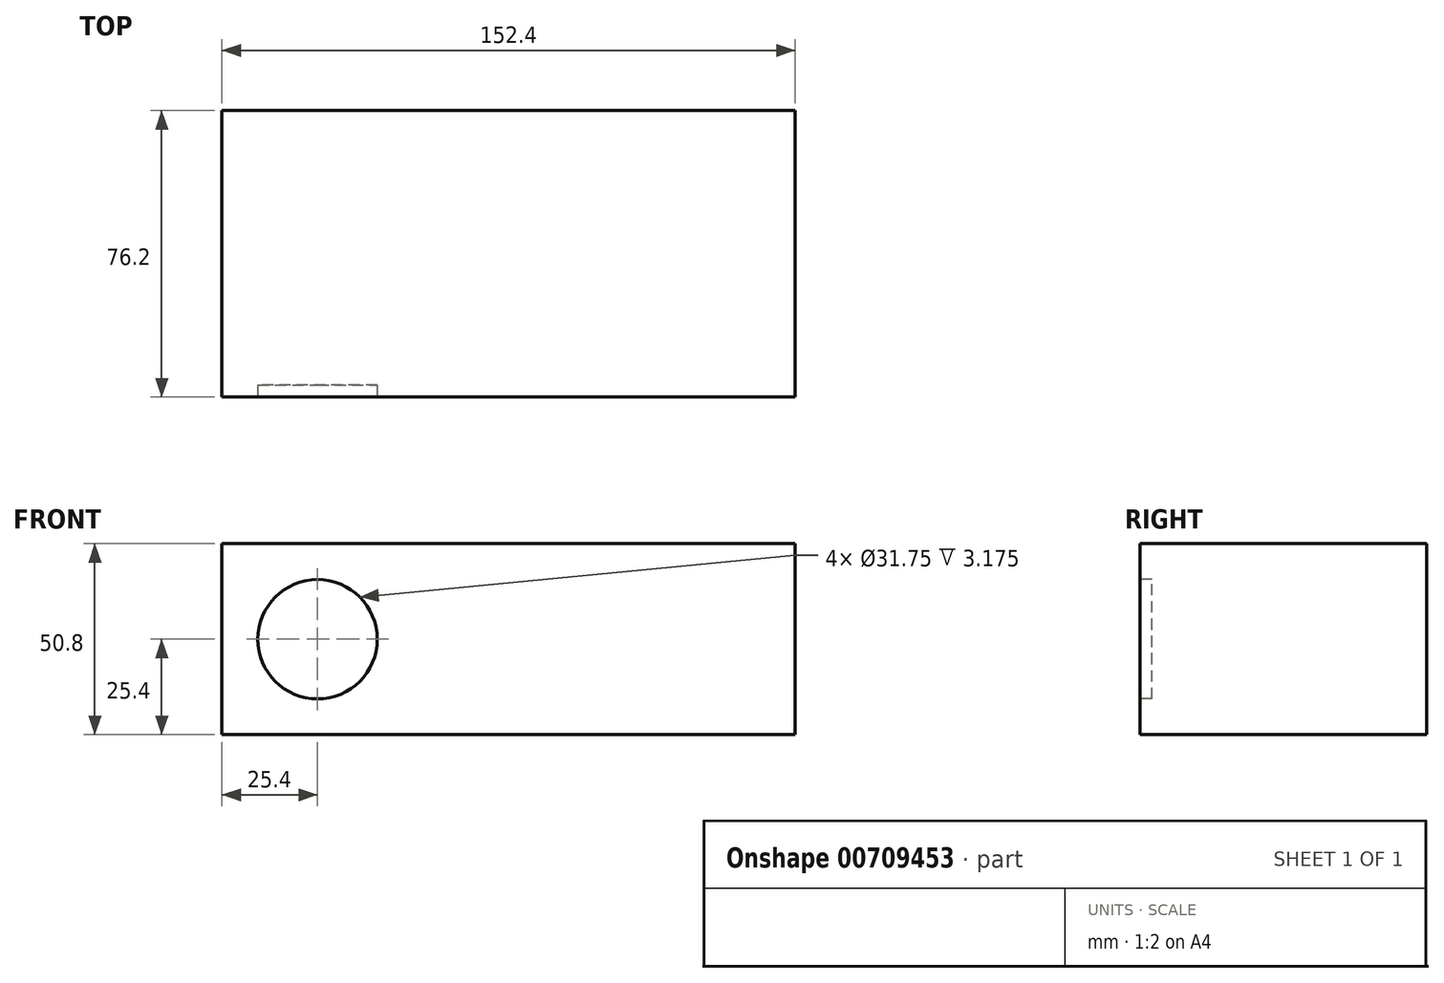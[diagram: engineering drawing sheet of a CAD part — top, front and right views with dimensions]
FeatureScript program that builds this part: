
annotation { "Feature Type Name" : "Feature", "Feature Type Description" : "" }
export const myFeature = defineFeature(function(context is Context, id is Id, definition is map)
    precondition{}
    {
        {
            var Q0;
            Q0=qCreatedBy(makeId("Front.planeOp"),FACE);
            var sketch = newSketch(context, id + "F0", { "sketchPlane" : qUnion([Q0])});
            skLineSegment(sketch, "E0.bottom", {"start": v(76.2, -25.4) * mm, "end": v(-76.2, -25.4) * mm});
            skLineSegment(sketch, "E0.top", {"start": v(76.2, 25.4) * mm, "end": v(-76.2, 25.4) * mm});
            skLineSegment(sketch, "E0.left", {"start": v(76.2, -25.4) * mm, "end": v(76.2, 25.4) * mm});
            skLineSegment(sketch, "E0.right", {"start": v(-76.2, -25.4) * mm, "end": v(-76.2, 25.4) * mm});
            skPoint(sketch, "E0.middle", {"position": v(0, 0) * mm});
            skSolve(sketch);
        }
        {
            var Q0;
            Q0=qSketchRegion(id+"F0",true);
            extrude(context, id + "F1", {"entities" : qUnion([Q0]), "depth" : 76.2 * mm, "offsetDistance" : 25.4 * mm});
        }
        {
            var Q0;
            Q0=makeQuery(id+"F1.opExtrude","CAP_FACE",FACE,{"disambiguationData":[OSD([sQuery(id+"F0.wireOp",EDGE,"E0.bottom"),sQuery(id+"F0.wireOp",EDGE,"E0.top"),sQuery(id+"F0.wireOp",EDGE,"E0.left"),sQuery(id+"F0.wireOp",EDGE,"E0.right")])],"isStart":false});
            var sketch = newSketch(context, id + "F2", { "sketchPlane" : qUnion([Q0])});
            skLineSegment(sketch, "E1", {"start": v(-50.8, 0) * mm, "end": v(-76.2, 0) * mm});
            skCircle(sketch, "E2", {"center": v(-50.8, 0) * mm, "radius": 15.88 * mm});
            skSolve(sketch);
        }
        {
            var Q0;
            Q0=qSketchRegion(id+"F2",true);
            extrude(context, id + "F3", {"entities" : qUnion([Q0]), "operationType" : NewBodyOperationType.REMOVE, "oppositeDirection" : true, "depth" : 3.17 * mm, "offsetDistance" : 25.4 * mm});
        }
    });
